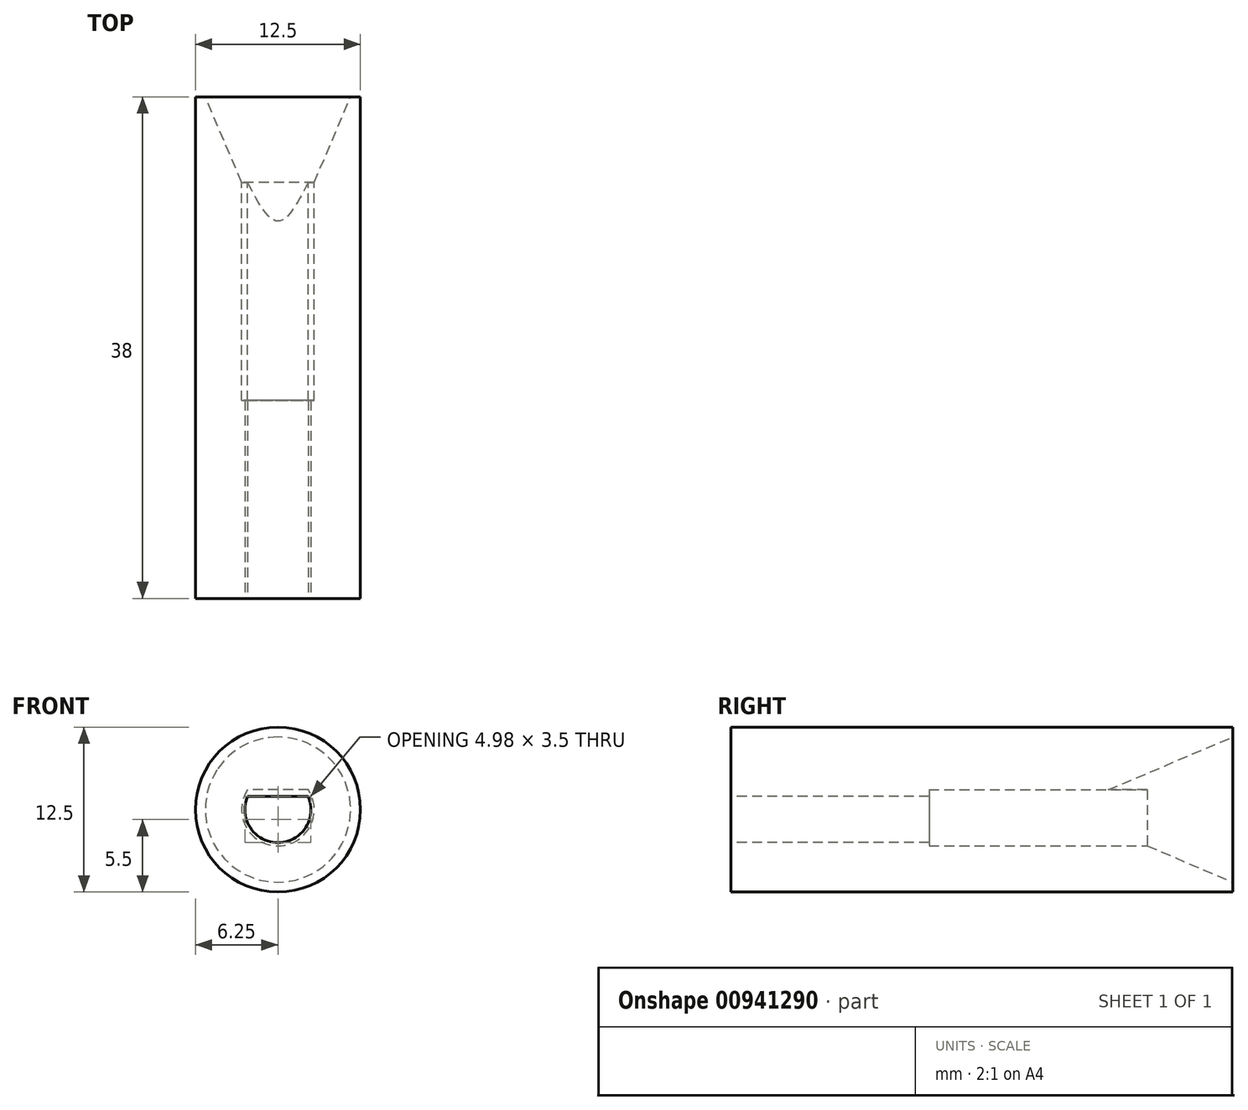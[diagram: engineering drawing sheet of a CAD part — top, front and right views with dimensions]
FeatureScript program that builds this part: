
annotation { "Feature Type Name" : "Feature", "Feature Type Description" : "" }
export const myFeature = defineFeature(function(context is Context, id is Id, definition is map)
    precondition{}
    {
        {
            var Q0;
            Q0=qCreatedBy(makeId("Front.planeOp"),FACE);
            var sketch = newSketch(context, id + "F0", { "sketchPlane" : qUnion([Q0])});
            skCircle(sketch, "E0", {"center": v(0, 0) * mm, "radius": 6.25 * mm});
            skSolve(sketch);
        }
        {
            var Q0;
            Q0 = qSketchRegion(id + "F0", true);
            extrude(context, id + "F1", {"entities" : qUnion([Q0]), "depth" : 38 * mm, "offsetDistance" : 25 * mm});
        }
        {
            var Q0;
            Q0=makeQuery(id+"F1.opExtrude","CAP_FACE",FACE,{"disambiguationData":[OSD([sQuery(id+"F0.wireOp",EDGE,"E0")])],"isStart":false});
            var sketch = newSketch(context, id + "F2", { "sketchPlane" : qUnion([Q0])});
            skArc(sketch, "E1", {"start": v(-2.3, 1) * mm, "mid": v(0, -2.5) * mm, "end": v(2.3, 1) * mm});
            skLineSegment(sketch, "E2", {"start": v(0, 0) * mm, "end": v(0, 1) * mm});
            skLineSegment(sketch, "E3", {"start": v(0, 1) * mm, "end": v(-2.3, 1) * mm});
            skLineSegment(sketch, "E4", {"start": v(-2.3, 1) * mm, "end": v(2.3, 1) * mm});
            skSolve(sketch);
        }
        {
            var Q0;
            Q0 = qSketchRegion(id + "F2", true);
            extrude(context, id + "F3", {"entities" : qUnion([Q0]), "operationType" : NewBodyOperationType.REMOVE, "oppositeDirection" : true, "depth" : 15 * mm, "offsetDistance" : 25 * mm});
        }
        {
            var Q0;
            Q0=makeQuery(id+"F1.opExtrude","CAP_FACE",FACE,{"disambiguationData":[OSD([sQuery(id+"F0.wireOp",EDGE,"E0")])],"isStart":true});
            var sketch = newSketch(context, id + "F4", { "sketchPlane" : qUnion([Q0])});
            skArc(sketch, "E5", {"start": v(-2.3, 1.5) * mm, "mid": v(0, -2.75) * mm, "end": v(2.3, 1.5) * mm});
            skLineSegment(sketch, "E6", {"start": v(0, 0) * mm, "end": v(0, 1.5) * mm});
            skLineSegment(sketch, "E7", {"start": v(0, 1.5) * mm, "end": v(-2.3, 1.5) * mm});
            skLineSegment(sketch, "E8", {"start": v(-2.3, 1.5) * mm, "end": v(2.3, 1.5) * mm});
            skSolve(sketch);
        }
        {
            var Q0;
            Q0 = qSketchRegion(id + "F4", true);
            extrude(context, id + "F5", {"entities" : qUnion([Q0]), "operationType" : NewBodyOperationType.REMOVE, "oppositeDirection" : true, "depth" : 23 * mm, "offsetDistance" : 25 * mm});
        }
        {
            var Q0;
            Q0=makeQuery(id+"F1.opExtrude","CAP_FACE",FACE,{"disambiguationData":[OSD([sQuery(id+"F0.wireOp",EDGE,"E0")])],"isStart":true});
            var sketch = newSketch(context, id + "F6", { "sketchPlane" : qUnion([Q0])});
            skCircle(sketch, "E9", {"center": v(0, 0) * mm, "radius": 5.5 * mm});
            skSolve(sketch);
        }
        {
            var Q0;
            Q0 = qSketchRegion(id + "F6", true);
            extrude(context, id + "F7", {"entities" : qUnion([Q0]), "operationType" : NewBodyOperationType.REMOVE, "oppositeDirection" : true, "depth" : 10 * mm, "offsetDistance" : 25 * mm, "hasDraft" : true, "draftAngle" : 23 * degree, "draftPullDirection" : true});
        }
    });
